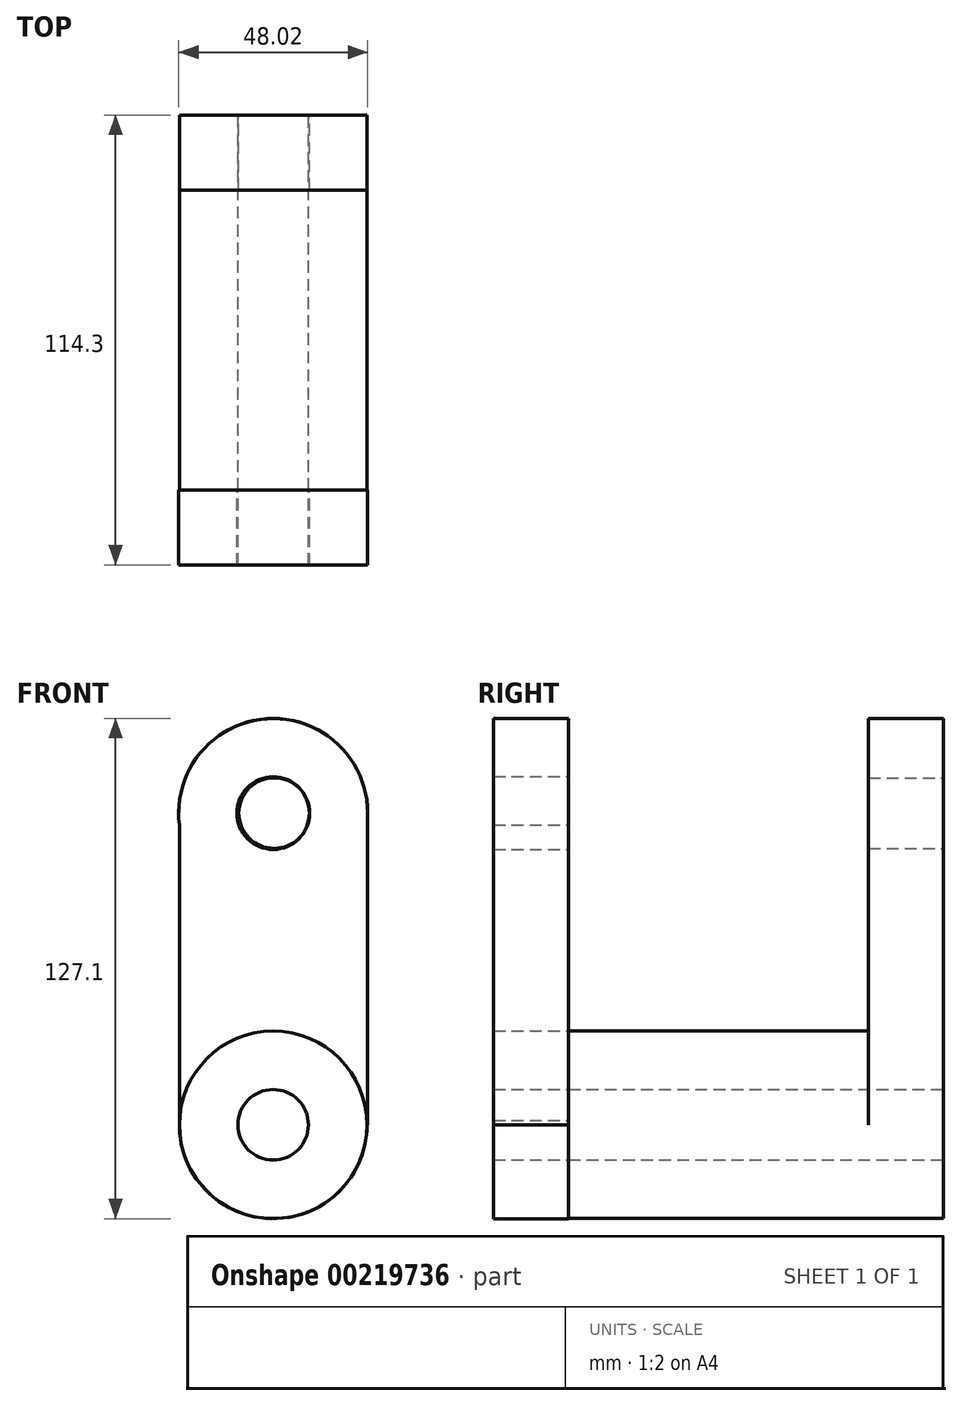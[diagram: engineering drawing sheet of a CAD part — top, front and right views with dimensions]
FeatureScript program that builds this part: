
annotation { "Feature Type Name" : "Feature", "Feature Type Description" : "" }
export const myFeature = defineFeature(function(context is Context, id is Id, definition is map)
    precondition{}
    {
        {
            var Q0;
            Q0=qCreatedBy(makeId("Front.planeOp"),FACE);
            var sketch = newSketch(context, id + "F0", { "sketchPlane" : qUnion([Q0])});
            skArc(sketch, "E0", {"start": v(-23.82, -30.83) * mm, "mid": v(0, -54.65) * mm, "end": v(23.82, -30.83) * mm});
            skLineSegment(sketch, "E1.left", {"start": v(23.82, -30.83) * mm, "end": v(23.82, 48.6) * mm});
            skLineSegment(sketch, "E1.right", {"start": v(-23.82, -30.83) * mm, "end": v(-23.82, 48.6) * mm});
            skPoint(sketch, "E1.middle", {"position": v(0, 8.9) * mm});
            skArc(sketch, "E2", {"start": v(23.82, 48.6) * mm, "mid": v(0, 72.43) * mm, "end": v(-23.82, 48.6) * mm});
            skCircle(sketch, "E3", {"center": v(0, -30.83) * mm, "radius": 8.97 * mm});
            skCircle(sketch, "E4", {"center": v(0.23, 48.38) * mm, "radius": 8.97 * mm});
            skSolve(sketch);
        }
        {
            var Q0;
            Q0=makeQuery(id+"F0.imprint","IMPRINT",FACE,{"disambiguationData":[TD([[makeQuery(id+"F0.imprint","IMPRINT",EDGE,{"derivedFrom":sQuery(id+"F0.wireOp",EDGE,"E0")}),1.0]])]});
            extrude(context, id + "F1", {"entities" : qUnion([Q0]), "depth" : 19.05 * mm});
        }
        {
            var Q0;
            Q0=makeQuery(id+"F1.opExtrude","CAP_FACE",FACE,{"disambiguationData":[OSD([sQuery(id+"F0.wireOp",EDGE,"E0"),sQuery(id+"F0.wireOp",EDGE,"E1.left"),sQuery(id+"F0.wireOp",EDGE,"E1.right"),sQuery(id+"F0.wireOp",EDGE,"E2"),sQuery(id+"F0.wireOp",EDGE,"E3"),sQuery(id+"F0.wireOp",EDGE,"E4")])],"isStart":false});
            var sketch = newSketch(context, id + "F2", { "sketchPlane" : qUnion([Q0])});
            skCircle(sketch, "E5", {"center": v(0, -30.83) * mm, "radius": 23.82 * mm});
            skSolve(sketch);
        }
        {
            var Q0;
            Q0=makeQuery(id+"F2.imprint","IMPRINT",FACE,{"disambiguationData":[TD([[makeQuery(id+"F2.imprint","IMPRINT",EDGE,{"derivedFrom":makeQuery(id+"F1.opExtrude","CAP_EDGE",EDGE,{"disambiguationData":[OSD([sQuery(id+"F0.wireOp",EDGE,"E3")])],"isStart":false})}),-1.0]])]});
            extrude(context, id + "F3", {"entities" : qUnion([Q0]), "operationType" : NewBodyOperationType.ADD, "depth" : 76.2 * mm});
        }
        {
            var Q0;
            Q0=makeQuery(id+"F3.opExtrude","CAP_FACE",FACE,{"disambiguationData":[OSD([sQuery(id+"F0.wireOp",EDGE,"E3"),sQuery(id+"F2.wireOp",EDGE,"E5")])],"isStart":false});
            var sketch = newSketch(context, id + "F4", { "sketchPlane" : qUnion([Q0])});
            skArc(sketch, "E6", {"start": v(-23.82, -29.76) * mm, "mid": v(-0.53, -54.66) * mm, "end": v(23.84, -30.83) * mm});
            skArc(sketch, "E7", {"start": v(-9.01, -30.83) * mm, "mid": v(0, -39.84) * mm, "end": v(9.01, -30.83) * mm});
            skLineSegment(sketch, "E8.bottom", {"start": v(23.84, -30.83) * mm, "end": v(24.01, -30.83) * mm});
            skLineSegment(sketch, "E8.left", {"start": v(-23.82, -30.83) * mm, "end": v(-23.82, 48.38) * mm});
            skLineSegment(sketch, "E8.right", {"start": v(24.01, -30.83) * mm, "end": v(24.01, 48.38) * mm});
            skArc(sketch, "E9", {"start": v(24.01, 48.38) * mm, "mid": v(-1.53, 72.34) * mm, "end": v(-23.82, 45.33) * mm});
            skCircle(sketch, "E10", {"center": v(0, 48.38) * mm, "radius": 9.24 * mm});
            skSolve(sketch);
        }
        {
            var Q0;
            {var subQ2=sQuery(id+"F4.wireOp",EDGE,"E6");Q0=makeQuery(id+"F4.imprint","IMPRINT",FACE,{"disambiguationData":[TD([[makeQuery(id+"F4.imprint","IMPRINT",EDGE,{"derivedFrom":subQ2}),1.0]])]});}
            extrude(context, id + "F5", {"entities" : qUnion([Q0]), "depth" : 19.05 * mm});
        }
        {
            var Q0;
            Q0=makeQuery(id+"F3.opExtrude","CAP_FACE",FACE,{"disambiguationData":[OSD([sQuery(id+"F0.wireOp",EDGE,"E3"),sQuery(id+"F2.wireOp",EDGE,"E5")])],"isStart":false});
            extrude(context, id + "F6", {"entities" : qUnion([Q0]), "depth" : 19.05 * mm});
        }
    });
